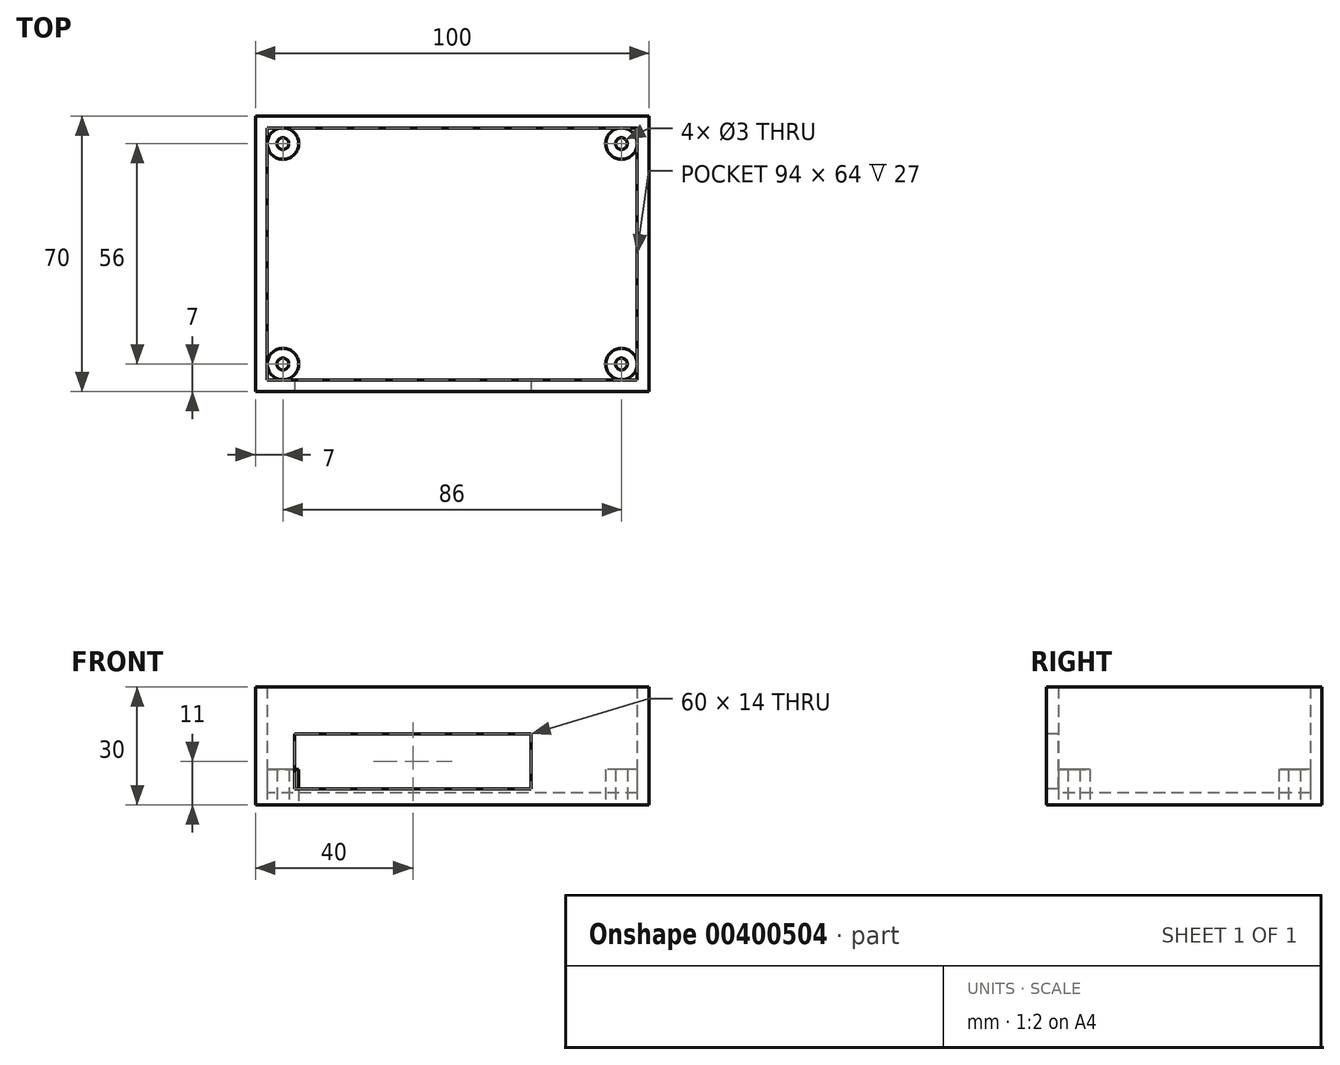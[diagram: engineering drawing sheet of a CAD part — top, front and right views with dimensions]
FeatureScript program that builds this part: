
annotation { "Feature Type Name" : "Feature", "Feature Type Description" : "" }
export const myFeature = defineFeature(function(context is Context, id is Id, definition is map)
    precondition{}
    {
        {
            var Q0;
            Q0=qCreatedBy(makeId("Top.planeOp"),FACE);
            var sketch = newSketch(context, id + "F0", { "sketchPlane" : qUnion([Q0])});
            skLineSegment(sketch, "E0.bottom", {"start": v(50, 35) * mm, "end": v(-50, 35) * mm});
            skLineSegment(sketch, "E0.top", {"start": v(50, -35) * mm, "end": v(-50, -35) * mm});
            skLineSegment(sketch, "E0.left", {"start": v(50, 35) * mm, "end": v(50, -35) * mm});
            skLineSegment(sketch, "E0.right", {"start": v(-50, 35) * mm, "end": v(-50, -35) * mm});
            skPoint(sketch, "E0.middle", {"position": v(0, 0) * mm});
            skSolve(sketch);
        }
        {
            var Q0;
            Q0=makeQuery(id+"F0.imprint","IMPRINT",FACE,{"disambiguationData":[TD([[makeQuery(id+"F0.imprint","IMPRINT",EDGE,{"derivedFrom":sQuery(id+"F0.wireOp",EDGE,"E0.bottom")}),1.0]])]});
            extrude(context, id + "F1", {"entities" : qUnion([Q0]), "depth" : 30 * mm});
        }
        {
            var Q0;
            Q0=makeQuery(id+"F1.opExtrude","CAP_FACE",FACE,{"disambiguationData":[OSD([sQuery(id+"F0.wireOp",EDGE,"E0.bottom"),sQuery(id+"F0.wireOp",EDGE,"E0.top"),sQuery(id+"F0.wireOp",EDGE,"E0.left"),sQuery(id+"F0.wireOp",EDGE,"E0.right")])],"isStart":false});
            shell(context, id + "F2", {"entities" : qUnion([Q0]), "thickness" : 3 * mm});
        }
        {
            var Q0;
            Q0=qCreatedBy(makeId("Top.planeOp"),FACE);
            var sketch = newSketch(context, id + "F3", { "sketchPlane" : qUnion([Q0])});
            skCircle(sketch, "E1", {"center": v(-43, 28) * mm, "radius": 4 * mm});
            skCircle(sketch, "E2.0", {"center": v(-43, 28) * mm, "radius": 1.5 * mm});
            skCircle(sketch, "E3.MirrorC", {"center": v(43, 28) * mm, "radius": 4 * mm});
            skCircle(sketch, "E4.MirrorC", {"center": v(43, 28) * mm, "radius": 1.5 * mm});
            skCircle(sketch, "E5.MirrorC", {"center": v(43, -28) * mm, "radius": 4 * mm});
            skCircle(sketch, "E6.MirrorC", {"center": v(43, -28) * mm, "radius": 1.5 * mm});
            skCircle(sketch, "E7.MirrorC", {"center": v(-43, -28) * mm, "radius": 1.5 * mm});
            skCircle(sketch, "E8.MirrorC", {"center": v(-43, -28) * mm, "radius": 4 * mm});
            skSolve(sketch);
        }
        {
            var Q0;
            Q0 = qSketchRegion(id + "F3", true);
            extrude(context, id + "F4", {"entities" : qUnion([Q0]), "depth" : 9 * mm});
        }
        {
            var Q0;
            Q0=makeQuery(id+"F1.opExtrude","SWEPT_FACE",FACE,{"disambiguationData":[OSD([sQuery(id+"F0.wireOp",EDGE,"E0.top")])]});
            var sketch = newSketch(context, id + "F5", { "sketchPlane" : qUnion([Q0])});
            skLineSegment(sketch, "E9.bottom", {"start": v(-40, 4) * mm, "end": v(20, 4) * mm});
            skLineSegment(sketch, "E9.top", {"start": v(-40, 18) * mm, "end": v(20, 18) * mm});
            skLineSegment(sketch, "E9.left", {"start": v(-40, 4) * mm, "end": v(-40, 18) * mm});
            skLineSegment(sketch, "E9.right", {"start": v(20, 4) * mm, "end": v(20, 18) * mm});
            skSolve(sketch);
        }
        {
            var Q0;
            Q0=makeQuery(id+"F5.imprint","IMPRINT",FACE,{"disambiguationData":[TD([[makeQuery(id+"F5.imprint","IMPRINT",EDGE,{"derivedFrom":sQuery(id+"F5.wireOp",EDGE,"E9.bottom")}),1.0]])]});
            extrude(context, id + "F6", {"entities" : qUnion([Q0]), "operationType" : NewBodyOperationType.REMOVE, "oppositeDirection" : true, "depth" : 3 * mm});
        }
    });
